annotation { "Feature Type Name" : "Feature", "Feature Type Description" : "" }
export const myFeature = defineFeature(function(context is Context, id is Id, definition is map)
    precondition{}
    {
        {
            var Q0;
            Q0=qCreatedBy(makeId("Top.planeOp"),FACE);
            var sketch = newSketch(context, id + "F0", { "sketchPlane" : qUnion([Q0])});
            skLineSegment(sketch, "E0.bottom", {"start": v(-93, 53) * mm, "end": v(3, 53) * mm});
            skLineSegment(sketch, "E0.top", {"start": v(-90, 0) * mm, "end": v(0, 0) * mm});
            skLineSegment(sketch, "E0.left", {"start": v(-93, 53) * mm, "end": v(-93, 43) * mm});
            skLineSegment(sketch, "E0.right", {"start": v(3, 53) * mm, "end": v(3, 43) * mm});
            skPoint(sketch, "E0.middle", {"position": v(0, 0) * mm});
            skLineSegment(sketch, "E1", {"start": v(-93, 43) * mm, "end": v(-90, 43) * mm});
            skLineSegment(sketch, "E2", {"start": v(-90, 43) * mm, "end": v(-90, 0) * mm});
            skLineSegment(sketch, "E3", {"start": v(0, 0) * mm, "end": v(0, 43) * mm});
            skLineSegment(sketch, "E4", {"start": v(0, 43) * mm, "end": v(3, 43) * mm});
            skSolve(sketch);
        }
        {
            var Q0;
            Q0=makeQuery(id+"F0.imprint","IMPRINT",FACE,{"disambiguationData":[TD([[makeQuery(id+"F0.imprint","IMPRINT",EDGE,{"derivedFrom":sQuery(id+"F0.wireOp",EDGE,"E0.bottom")}),-1.0]])]});
            extrude(context, id + "F1", {"entities" : qUnion([Q0]), "depth" : 3 * mm, "offsetDistance" : 25 * mm});
        }
        {
            var Q0;
            Q0=makeQuery(id+"F1.opExtrude","CAP_FACE",FACE,{"disambiguationData":[OSD([sQuery(id+"F0.wireOp",EDGE,"E0.bottom"),sQuery(id+"F0.wireOp",EDGE,"E0.top"),sQuery(id+"F0.wireOp",EDGE,"E0.left"),sQuery(id+"F0.wireOp",EDGE,"E0.right")])],"isStart":false});
            var sketch = newSketch(context, id + "F2", { "sketchPlane" : qUnion([Q0])});
            skLineSegment(sketch, "E5.bottom", {"start": v(-93, 53) * mm, "end": v(3, 53) * mm});
            skLineSegment(sketch, "E5.left", {"start": v(-93, 53) * mm, "end": v(-93, 43) * mm});
            skLineSegment(sketch, "E5.right", {"start": v(3, 53) * mm, "end": v(3, 43) * mm});
            skLineSegment(sketch, "E6.0", {"start": v(-90.5, 50.5) * mm, "end": v(0.5, 50.5) * mm});
            skLineSegment(sketch, "E6.1", {"start": v(-90.5, 50.5) * mm, "end": v(-90.5, 43) * mm});
            skLineSegment(sketch, "E6.3", {"start": v(0.5, 50.5) * mm, "end": v(0.5, 43) * mm});
            skLineSegment(sketch, "E7", {"start": v(-93, 43) * mm, "end": v(-90.5, 43) * mm});
            skLineSegment(sketch, "E8", {"start": v(0.5, 43) * mm, "end": v(3, 43) * mm});
            skSolve(sketch);
        }
        {
            var Q0;
            Q0 = qSketchRegion(id + "F2", true);
            extrude(context, id + "F3", {"entities" : qUnion([Q0]), "operationType" : NewBodyOperationType.ADD, "depth" : 2 * mm, "offsetDistance" : 25 * mm});
        }
        {
            var Q0;
            Q0=makeQuery(id+"F1.opExtrude","CAP_FACE",FACE,{"disambiguationData":[OSD([sQuery(id+"F0.wireOp",EDGE,"E0.bottom"),sQuery(id+"F0.wireOp",EDGE,"E0.top"),sQuery(id+"F0.wireOp",EDGE,"E0.left"),sQuery(id+"F0.wireOp",EDGE,"E0.right"),sQuery(id+"F0.wireOp",EDGE,"E1"),sQuery(id+"F0.wireOp",EDGE,"E2"),sQuery(id+"F0.wireOp",EDGE,"E3"),sQuery(id+"F0.wireOp",EDGE,"E4")])],"isStart":false});
            var sketch = newSketch(context, id + "F4", { "sketchPlane" : qUnion([Q0])});
            skText(sketch, "E9", { "text": "SolidCAM", "fontName": "RobotoSlab-Bold.ttf"});
            skText(sketch, "E10", { "text": "Avi Zulti\nSoftware Architect", "fontName": "Tinos-Bold.ttf"});
            skText(sketch, "E11", { "text": "PROBLEM\nSOLVED !", "fontName": "OpenSans-Bold.ttf"});
            skText(sketch, "E12", { "text": "<email>", "fontName": "Arimo-Regular.ttf"});
            skText(sketch, "E13", { "text": "CREATE\nPROBLEMS", "fontName": "OpenSans-Bold.ttf"});
            const initialGuessF4  = {"E9": [-0.02622, 0.03942, 1, 0, 0.00358], "E10": [-0.07978, 0.03848, 1, 0, 0.00523], "E11": [-0.07963, 0.02363, 0.8935, -0.44907, 0.00362], "E12": [-0.06252, 0.00266, 1, 0, 0.0037], "E13": [-0.03437, 0.0161, 0.9464, 0.32297, 0.00362]};
            skSetInitialGuess(sketch, initialGuessF4);
            skSolve(sketch);
        }
        {
            var Q0;
            Q0 = qSketchRegion(id + "F4", true);
            extrude(context, id + "F5", {"entities" : qUnion([Q0]), "operationType" : NewBodyOperationType.ADD, "depth" : 2 * mm, "offsetDistance" : 25 * mm});
        }
        {
            var Q0;
            Q0=makeQuery(id+"F3.opExtrude","CAP_FACE",FACE,{"disambiguationData":[OSD([sQuery(id+"F2.wireOp",EDGE,"E5.bottom"),sQuery(id+"F2.wireOp",EDGE,"E5.left"),sQuery(id+"F2.wireOp",EDGE,"E5.right"),sQuery(id+"F2.wireOp",EDGE,"E6.0"),sQuery(id+"F2.wireOp",EDGE,"E6.1"),sQuery(id+"F2.wireOp",EDGE,"E6.3"),sQuery(id+"F2.wireOp",EDGE,"E7"),sQuery(id+"F2.wireOp",EDGE,"E8")])],"isStart":false});
            var sketch = newSketch(context, id + "F6", { "sketchPlane" : qUnion([Q0])});
            skLineSegment(sketch, "E14", {"start": v(-93, 43) * mm, "end": v(-93, -3) * mm});
            skLineSegment(sketch, "E15", {"start": v(-93, -3) * mm, "end": v(3, -3) * mm});
            skLineSegment(sketch, "E16", {"start": v(3, -3) * mm, "end": v(3, 43) * mm});
            skLineSegment(sketch, "E17", {"start": v(3, 43) * mm, "end": v(0, 43) * mm});
            skLineSegment(sketch, "E18", {"start": v(-93, 43) * mm, "end": v(-90, 43) * mm});
            skPoint(sketch, "E18.endSnap0", {"position": v(-91.75, 43) * mm});
            skLineSegment(sketch, "E19", {"start": v(-90, 43) * mm, "end": v(-90, 50) * mm});
            skLineSegment(sketch, "E20", {"start": v(-90, 50) * mm, "end": v(0, 50) * mm});
            skLineSegment(sketch, "E21", {"start": v(0, 50) * mm, "end": v(0, 43) * mm});
            skSolve(sketch);
        }
        {
            var Q0;
            Q0 = qSketchRegion(id + "F6", true);
            extrude(context, id + "F7", {"entities" : qUnion([Q0]), "depth" : 3 * mm, "offsetDistance" : 25 * mm});
        }
        {
            var Q0;
            Q0=makeQuery(id+"F7.opExtrude","CAP_FACE",FACE,{"disambiguationData":[OSD([sQuery(id+"F6.wireOp",EDGE,"E14"),sQuery(id+"F6.wireOp",EDGE,"E15"),sQuery(id+"F6.wireOp",EDGE,"E16"),sQuery(id+"F6.wireOp",EDGE,"E17"),sQuery(id+"F6.wireOp",EDGE,"E18"),sQuery(id+"F6.wireOp",EDGE,"E19"),sQuery(id+"F6.wireOp",EDGE,"E20"),sQuery(id+"F6.wireOp",EDGE,"E21")])],"isStart":true});
            var sketch = newSketch(context, id + "F8", { "sketchPlane" : qUnion([Q0])});
            skLineSegment(sketch, "E22", {"start": v(-93, -43) * mm, "end": v(-90.5, -43) * mm});
            skPoint(sketch, "E22.endSnap0", {"position": v(-91.5, -43) * mm});
            skLineSegment(sketch, "E23", {"start": v(-90.5, -43) * mm, "end": v(-90.5, 0.5) * mm});
            skLineSegment(sketch, "E24", {"start": v(-90.5, 0.5) * mm, "end": v(0.5, 0.5) * mm});
            skLineSegment(sketch, "E25", {"start": v(0.5, 0.5) * mm, "end": v(0.5, -43) * mm});
            skLineSegment(sketch, "E26", {"start": v(0.5, -43) * mm, "end": v(3, -43) * mm});
            skLineSegment(sketch, "E27", {"start": v(3, -43) * mm, "end": v(3, 3) * mm});
            skLineSegment(sketch, "E28", {"start": v(3, 3) * mm, "end": v(-93, 3) * mm});
            skLineSegment(sketch, "E29", {"start": v(-93, 3) * mm, "end": v(-93, -43) * mm});
            skSolve(sketch);
        }
        {
            var Q0;
            Q0 = qSketchRegion(id + "F8", true);
            extrude(context, id + "F9", {"entities" : qUnion([Q0]), "operationType" : NewBodyOperationType.ADD, "depth" : 2 * mm, "offsetDistance" : 25 * mm});
        }
        {
            var Q0;
            Q0 = qSketchRegion(id + "F4", true);
            extrude(context, id + "F10", {"entities" : qUnion([Q0]), "operationType" : NewBodyOperationType.REMOVE, "depth" : 3.5 * mm, "offsetDistance" : 25 * mm});
        }
    });